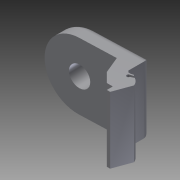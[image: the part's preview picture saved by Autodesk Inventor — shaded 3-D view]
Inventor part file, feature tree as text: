
AUTODESK INVENTOR PART (.ipt)
format: ipt  version: 2012 (Build 160160000, 160)  size: 160,768 bytes
history: native  units: mm
features: fillet x3, chamfer x3, extrude x2, sketch x2
ambient origin geometry x8: Origin, YZ Plane, XZ Plane, XY Plane, X Axis, Y Axis, Z Axis, Center Point
bodies: Solid1 (feature_tree)
feature tree (10):
  extrude  "Extrusion1"  Depth=5.0mm
  fillet  "Fillet1"  Radius=5.0mm
  fillet  "Fillet2"  Radius=1.8mm
  extrude  "Extrusion2"  Depth=1.8mm
  fillet  "Fillet3"  Radius=20.0mm
  chamfer  "Chamfer2"  Distance=4.0mm
  chamfer  "Chamfer3"  Distance=10.0mm
  chamfer  "Chamfer4"  Distance=6.2mm
  sketch  "Sketch1"  dims[d0=21.0mm d1=5.0mm d2=5.0mm d4=1.8mm]
  sketch  "Sketch2"  dims[d5=6.0mm d6=1.8mm d9=20.0mm d10=0.0mm d11=4.0mm d12=10.0mm d16=6.2mm d17=10.0mm d18=0.0mm d19=2.0mm d22=5.0mm d23=2.0mm d24=45.0deg d25=3.0mm d26=2.0mm d27=45.0deg d28=0.5mm d29=2.0mm d30=45.0deg d31=15.358897mm d32=8.0mm d33=10.0mm d34=0.0mm d35=19.198622mm d36=1.0mm d37=4.0mm d38=6.0mm d40=0.4mm d41=4.0mm d42=2.0mm d44=1.2mm d45=1.0mm]
